# Revit family: Reneo-Fit D 100
name_source: partatom
category: Mechanical Equipment
units: mm (PartAtom-declared; Revit-internal decimal feet)

## family parameters
Always vertical = Yes
Classification = None
Cut with Voids When Loaded = No
Part Type = Normal
Room Calculation Point = No
Round Connector Dimension = Use Diameter
Shared = No
Work Plane-Based = No

## types (2) — shared parameters
00_20_Manufacturer = Blauberg
00_20_Name = Energy recovery ventilator
Amperage = 0.340 A
Casing Material = Polypropylene (black)
D = 125 mm  [stored 0.410105 ft]
Diameter = 125 mm  [stored 0.410105 ft]
Filter = G4 / Coarse > 60%
H = 242 mm  [stored 0.793963 ft]
Height = 242 mm  [stored 0.793963 ft]
L = 530 mm  [stored 1.73885 ft]
Length = 530 mm  [stored 1.73885 ft]
Load Classification = HVAC
Maintenance zone material = <By Category>
Manufacturer = Blauberg
Maximum Air Flow = 130.0 m³/h
Number of Fase = 1
Power = 38 W
Pressure_Static_Air = 0.0 Pa
Sound pressure level at 3 m distance = 32 dBA
Temperature of moving air = –23…+40°С
URL = https://blaubergventilatoren.de
Voltage = 230 V
W = 520 mm  [stored 1.70604 ft]
Weight = 8.00 kg
Width = 520 mm  [stored 1.70604 ft]
d = 115 mm  [stored 0.377297 ft]
l = 420 mm  [stored 1.37795 ft]
w = 410 mm  [stored 1.34514 ft]
zero-valued in all types: Default Elevation

## type names (no varying parameters)
- Reneo-Fit D 100 S14
- Reneo-Fit D 100-E S14

note: column(s) folded — value = type name in every type: 00_20_Type

note: [stored X ft] marks values corroborated as IEEE doubles in the binary element streams (Revit-internal decimal feet)
